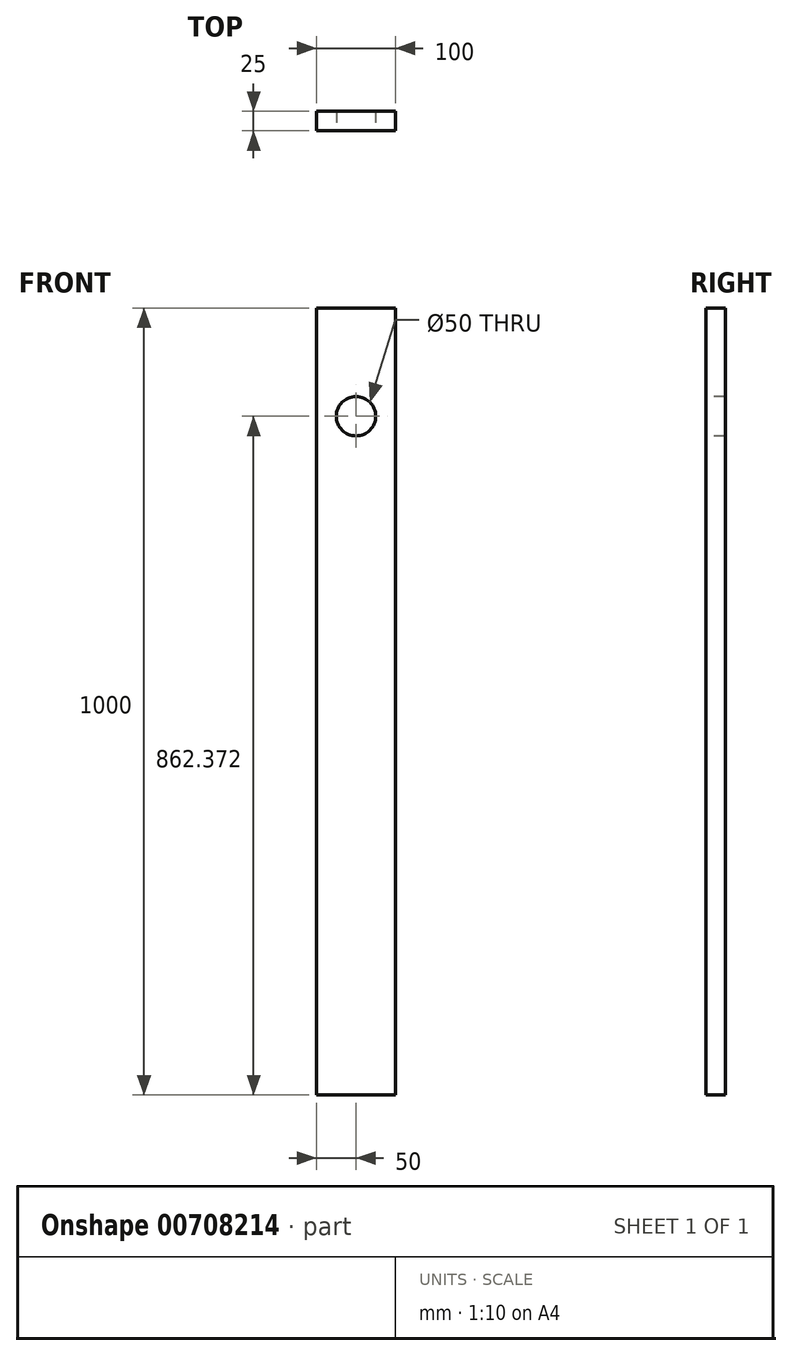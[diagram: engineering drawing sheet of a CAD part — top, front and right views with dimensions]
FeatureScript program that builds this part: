
annotation { "Feature Type Name" : "Feature", "Feature Type Description" : "" }
export const myFeature = defineFeature(function(context is Context, id is Id, definition is map)
    precondition{}
    {
        {
            var Q0;
            Q0=qCreatedBy(makeId("Front.planeOp"),FACE);
            var sketch = newSketch(context, id + "F0", { "sketchPlane" : qUnion([Q0])});
            skLineSegment(sketch, "E0.bottom", {"start": v(0, 0) * mm, "end": v(100, 0) * mm});
            skLineSegment(sketch, "E0.top", {"start": v(0, 1000) * mm, "end": v(100, 1000) * mm});
            skLineSegment(sketch, "E0.left", {"start": v(0, 0) * mm, "end": v(0, 1000) * mm});
            skLineSegment(sketch, "E0.right", {"start": v(100, 0) * mm, "end": v(100, 1000) * mm});
            skSolve(sketch);
        }
        {
            var Q0;
            Q0=makeQuery(id+"F0.imprint","IMPRINT",FACE,{"disambiguationData":[TD([[makeQuery(id+"F0.imprint","IMPRINT",EDGE,{"derivedFrom":sQuery(id+"F0.wireOp",EDGE,"E0.bottom")}),1.0]])]});
            extrude(context, id + "F1", {"entities" : qUnion([Q0]), "depth" : 25 * mm, "offsetDistance" : 25 * mm});
        }
        {
            var Q0;
            Q0=makeQuery(id+"F1.opExtrude","CAP_FACE",FACE,{"disambiguationData":[OSD([sQuery(id+"F0.wireOp",EDGE,"E0.bottom"),sQuery(id+"F0.wireOp",EDGE,"E0.top"),sQuery(id+"F0.wireOp",EDGE,"E0.left"),sQuery(id+"F0.wireOp",EDGE,"E0.right")])],"isStart":false});
            var sketch = newSketch(context, id + "F2", { "sketchPlane" : qUnion([Q0])});
            skCircle(sketch, "E1", {"center": v(50, 862.37) * mm, "radius": 25 * mm});
            skPoint(sketch, "E1.centerSnap0", {"position": v(50, 1000) * mm});
            skSolve(sketch);
        }
        {
            var Q0;
            Q0=makeQuery(id+"F2.imprint","IMPRINT",FACE,{"disambiguationData":[TD([[makeQuery(id+"F2.imprint","IMPRINT",EDGE,{"derivedFrom":sQuery(id+"F2.wireOp",EDGE,"E1")}),1.0]])]});
            extrude(context, id + "F3", {"entities" : qUnion([Q0]), "operationType" : NewBodyOperationType.REMOVE, "endBound" : BoundingType.THROUGH_ALL, "oppositeDirection" : true, "depth" : 25 * mm, "offsetDistance" : 25 * mm});
        }
    });
